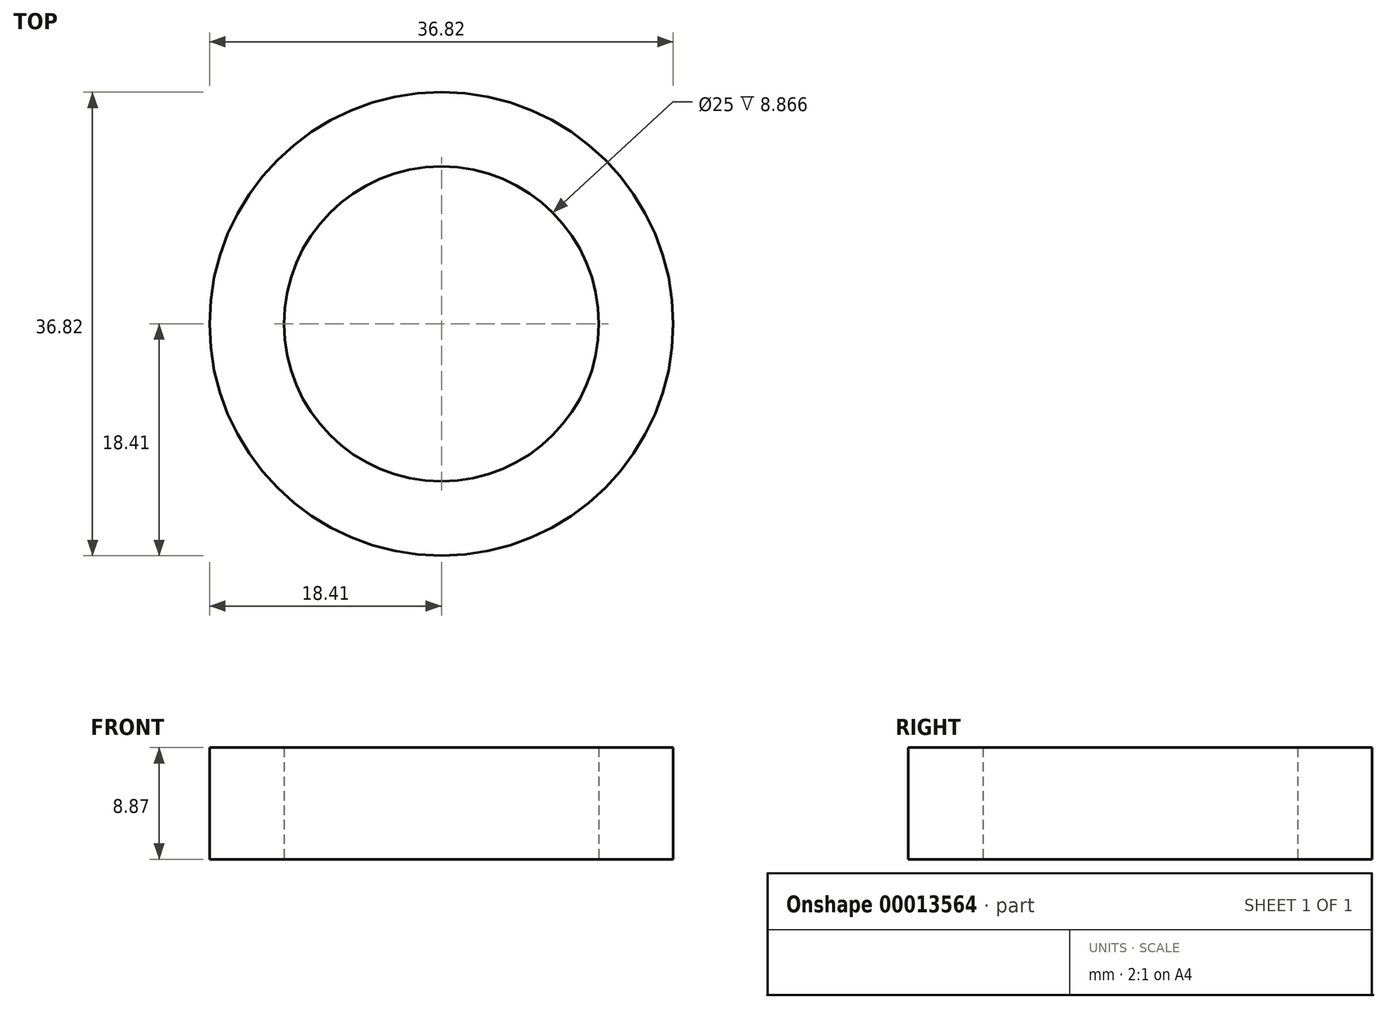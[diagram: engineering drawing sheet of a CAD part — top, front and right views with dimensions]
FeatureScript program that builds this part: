
annotation { "Feature Type Name" : "Feature", "Feature Type Description" : "" }
export const myFeature = defineFeature(function(context is Context, id is Id, definition is map)
    precondition{}
    {
        {
            var Q0;
            Q0=qCreatedBy(makeId("Front.planeOp"),FACE);
            var sketch = newSketch(context, id + "F0", { "sketchPlane" : qUnion([Q0])});
            skLineSegment(sketch, "E0", {"start": v(0, 0) * mm, "end": v(0, 16.6) * mm, "construction": true});
            skLineSegment(sketch, "E1", {"start": v(-18.41, 0) * mm, "end": v(-18.41, 8.87) * mm});
            skLineSegment(sketch, "E2", {"start": v(-18.41, 8.87) * mm, "end": v(-12.5, 8.87) * mm});
            skLineSegment(sketch, "E3", {"start": v(-12.5, 8.87) * mm, "end": v(-12.5, 0) * mm});
            skLineSegment(sketch, "E4", {"start": v(-12.5, 0) * mm, "end": v(-18.41, 0) * mm});
            skSolve(sketch);
        }
        {
            var Q0;
            Q0=makeQuery(id+"F0.imprint","IMPRINT",FACE,{"disambiguationData":[TD([[makeQuery(id+"F0.imprint","IMPRINT",EDGE,{"derivedFrom":sQuery(id+"F0.wireOp",EDGE,"E1")}),-1.0]])]});
            var Q1;
            Q1=sQuery(id+"F0.wireOp",EDGE,"E0");
            revolve(context, id + "F1", {"entities" : qUnion([Q0]), "axis" : qUnion([Q1]), "revolveType" : RevolveType.FULL});
        }
    });
